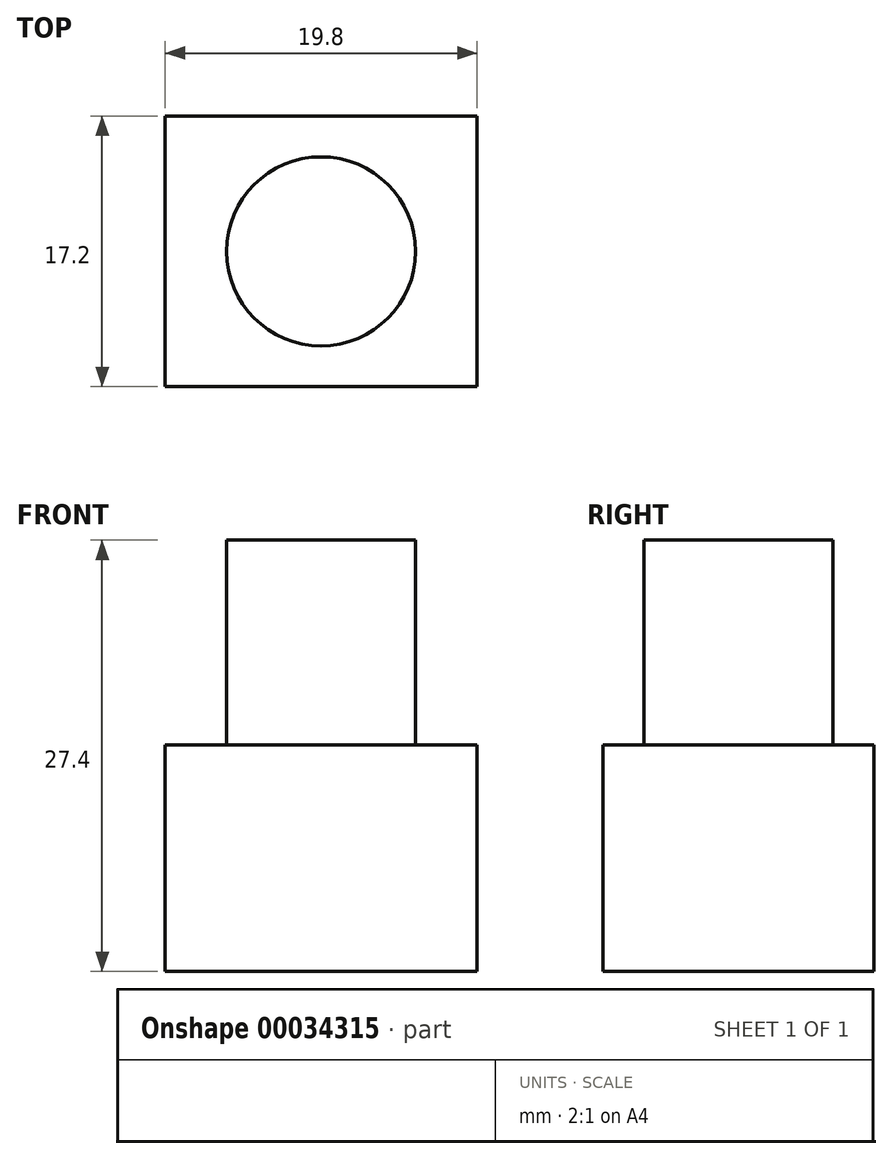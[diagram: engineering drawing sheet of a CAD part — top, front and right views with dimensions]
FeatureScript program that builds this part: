
annotation { "Feature Type Name" : "Feature", "Feature Type Description" : "" }
export const myFeature = defineFeature(function(context is Context, id is Id, definition is map)
    precondition{}
    {
        {
            var Q0;
            Q0=qCreatedBy(makeId("Top.planeOp"),FACE);
            var sketch = newSketch(context, id + "F0", { "sketchPlane" : qUnion([Q0])});
            skLineSegment(sketch, "E0.bottom", {"start": v(-6.8, -6.4) * mm, "end": v(13, -6.4) * mm});
            skLineSegment(sketch, "E0.top", {"start": v(-6.8, 10.8) * mm, "end": v(13, 10.8) * mm});
            skLineSegment(sketch, "E0.left", {"start": v(-6.8, -6.4) * mm, "end": v(-6.8, 10.8) * mm});
            skLineSegment(sketch, "E0.right", {"start": v(13, -6.4) * mm, "end": v(13, 10.8) * mm});
            skSolve(sketch);
        }
        {
            var Q0;
            Q0 = qSketchRegion(id + "F0", true);
            extrude(context, id + "F1", {"entities" : qUnion([Q0]), "depth" : 14.4 * mm});
        }
        {
            var Q0;
            Q0=makeQuery(id+"F1.opExtrude","CAP_FACE",FACE,{"disambiguationData":[OSD([sQuery(id+"F0.wireOp",EDGE,"E0.bottom"),sQuery(id+"F0.wireOp",EDGE,"E0.top"),sQuery(id+"F0.wireOp",EDGE,"E0.left"),sQuery(id+"F0.wireOp",EDGE,"E0.right")])],"isStart":false});
            var sketch = newSketch(context, id + "F2", { "sketchPlane" : qUnion([Q0])});
            skCircle(sketch, "E1", {"center": v(3.1, 2.2) * mm, "radius": 6 * mm});
            skPoint(sketch, "E1.centerSnap0", {"position": v(13, 2.2) * mm});
            skPoint(sketch, "E1.centerSnap1", {"position": v(3.1, 10.8) * mm});
            skSolve(sketch);
        }
        {
            var Q0;
            Q0 = qSketchRegion(id + "F2", true);
            extrude(context, id + "F3", {"entities" : qUnion([Q0]), "operationType" : NewBodyOperationType.ADD, "depth" : 13 * mm});
        }
    });
